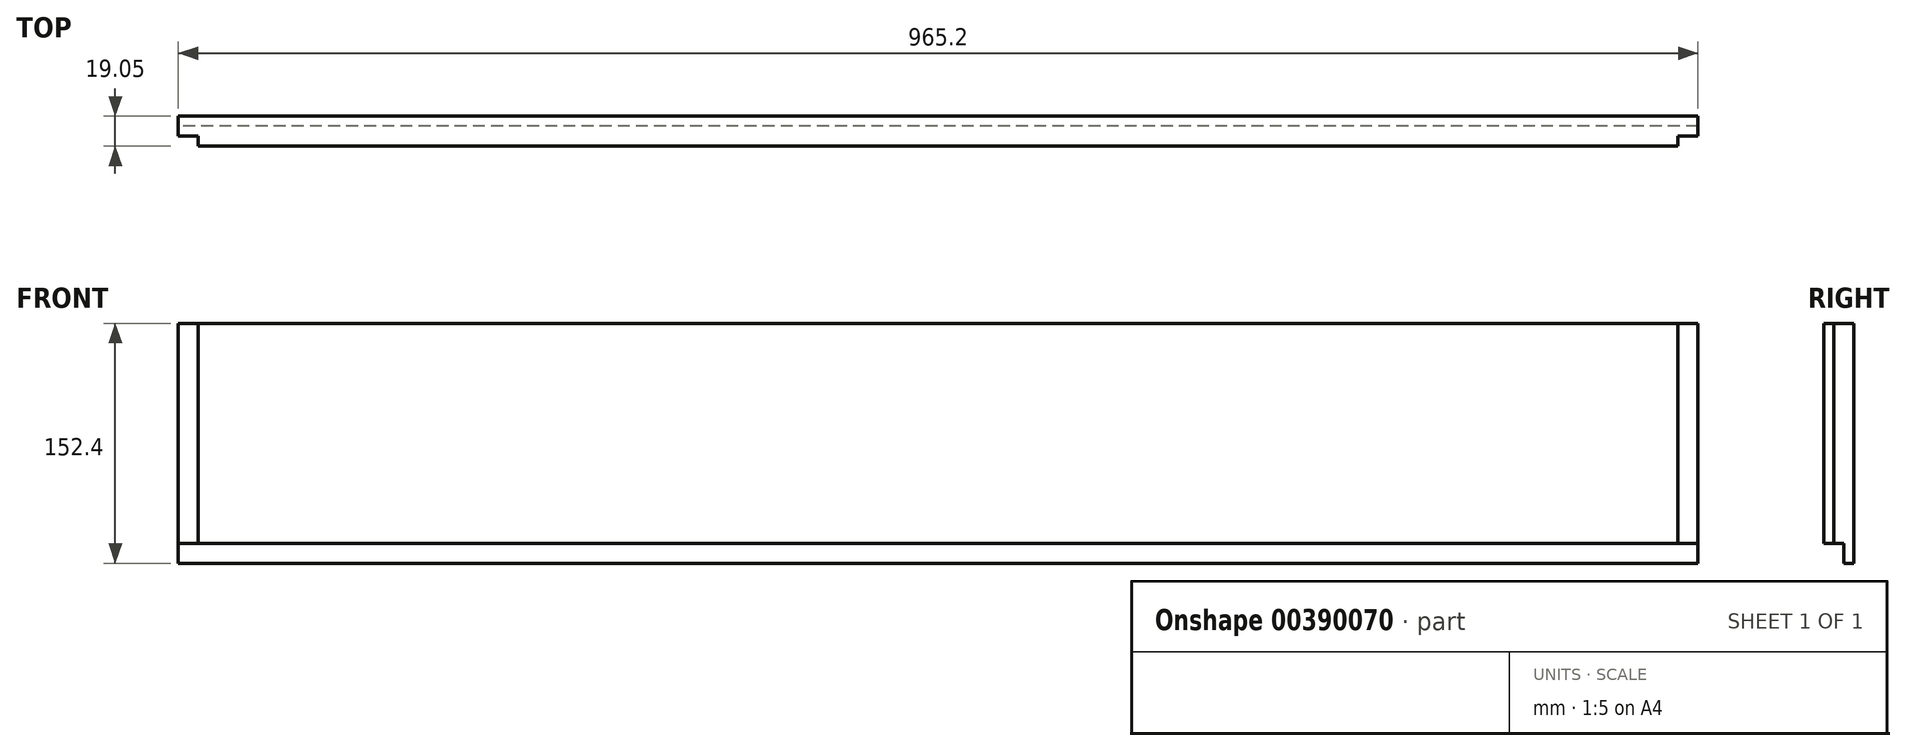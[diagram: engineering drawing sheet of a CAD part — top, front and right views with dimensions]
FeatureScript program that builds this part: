
annotation { "Feature Type Name" : "Feature", "Feature Type Description" : "" }
export const myFeature = defineFeature(function(context is Context, id is Id, definition is map)
    precondition{}
    {
        {
            var Q0;
            Q0=qCreatedBy(makeId("Front.planeOp"),FACE);
            var sketch = newSketch(context, id + "F0", { "sketchPlane" : qUnion([Q0])});
            skLineSegment(sketch, "E0", {"start": v(0, 0) * mm, "end": v(965.2, 0) * mm});
            skLineSegment(sketch, "E1", {"start": v(965.2, 0) * mm, "end": v(965.2, 152.4) * mm});
            skLineSegment(sketch, "E2", {"start": v(965.2, 152.4) * mm, "end": v(0, 152.4) * mm});
            skLineSegment(sketch, "E3", {"start": v(0, 152.4) * mm, "end": v(0, 0) * mm});
            skSolve(sketch);
        }
        {
            var Q0;
            Q0 = qSketchRegion(id + "F0", true);
            extrude(context, id + "F1", {"entities" : qUnion([Q0]), "depth" : 19.05 * mm});
        }
        {
            var Q0;
            Q0=makeQuery(id+"F1.opExtrude","SWEPT_FACE",FACE,{"disambiguationData":[OSD([sQuery(id+"F0.wireOp",EDGE,"E3")])]});
            var sketch = newSketch(context, id + "F2", { "sketchPlane" : qUnion([Q0])});
            skLineSegment(sketch, "E4", {"start": v(19.05, 0) * mm, "end": v(19.05, 12.7) * mm});
            skLineSegment(sketch, "E5", {"start": v(19.05, 12.7) * mm, "end": v(6.35, 12.7) * mm});
            skLineSegment(sketch, "E6", {"start": v(6.35, 12.7) * mm, "end": v(6.35, 0) * mm});
            skLineSegment(sketch, "E7", {"start": v(6.35, 0) * mm, "end": v(19.05, 0) * mm});
            skSolve(sketch);
        }
        {
            var Q0;
            Q0 = qSketchRegion(id + "F2", true);
            extrude(context, id + "F3", {"entities" : qUnion([Q0]), "operationType" : NewBodyOperationType.REMOVE, "endBound" : BoundingType.THROUGH_ALL, "oppositeDirection" : true, "depth" : 25.4 * mm});
        }
        {
            var Q0;
            Q0=makeQuery(id+"F1.opExtrude","SWEPT_FACE",FACE,{"disambiguationData":[OSD([sQuery(id+"F0.wireOp",EDGE,"E0")])]});
            var sketch = newSketch(context, id + "F4", { "sketchPlane" : qUnion([Q0])});
            skLineSegment(sketch, "E8", {"start": v(0, 0) * mm, "end": v(0, 19.05) * mm});
            skLineSegment(sketch, "E9", {"start": v(0, 19.05) * mm, "end": v(12.7, 19.05) * mm});
            skLineSegment(sketch, "E10", {"start": v(12.7, 19.05) * mm, "end": v(12.7, 12.7) * mm});
            skLineSegment(sketch, "E11", {"start": v(12.7, 12.7) * mm, "end": v(0, 12.7) * mm});
            skLineSegment(sketch, "E12", {"start": v(0, 12.7) * mm, "end": v(0, 19.05) * mm});
            skSolve(sketch);
        }
        {
            var Q0;
            Q0=makeQuery(id+"F4.imprint","IMPRINT",FACE,{"disambiguationData":[TD([[makeQuery(id+"F4.imprint","IMPRINT",EDGE,{"derivedFrom":sQuery(id+"F4.wireOp",EDGE,"E9")}),-1.0]])]});
            extrude(context, id + "F5", {"entities" : qUnion([Q0]), "operationType" : NewBodyOperationType.REMOVE, "endBound" : BoundingType.THROUGH_ALL, "oppositeDirection" : true, "depth" : 25.4 * mm});
        }
        {
            var Q0;
            Q0=makeQuery(id+"F1.opExtrude","SWEPT_FACE",FACE,{"disambiguationData":[OSD([sQuery(id+"F0.wireOp",EDGE,"E0")])]});
            var sketch = newSketch(context, id + "F6", { "sketchPlane" : qUnion([Q0])});
            skLineSegment(sketch, "E13", {"start": v(965.2, 0) * mm, "end": v(965.2, 19.05) * mm});
            skPoint(sketch, "E13.endSnap0", {"position": v(965.2, 3.18) * mm});
            skLineSegment(sketch, "E14", {"start": v(965.2, 19.05) * mm, "end": v(952.5, 19.05) * mm});
            skLineSegment(sketch, "E15", {"start": v(952.5, 19.05) * mm, "end": v(952.5, 12.7) * mm});
            skLineSegment(sketch, "E16", {"start": v(952.5, 12.7) * mm, "end": v(965.2, 12.7) * mm});
            skSolve(sketch);
        }
        {
            var Q0;
            Q0 = qSketchRegion(id + "F6", true);
            extrude(context, id + "F7", {"entities" : qUnion([Q0]), "operationType" : NewBodyOperationType.REMOVE, "endBound" : BoundingType.THROUGH_ALL, "oppositeDirection" : true, "depth" : 25.4 * mm});
        }
    });
